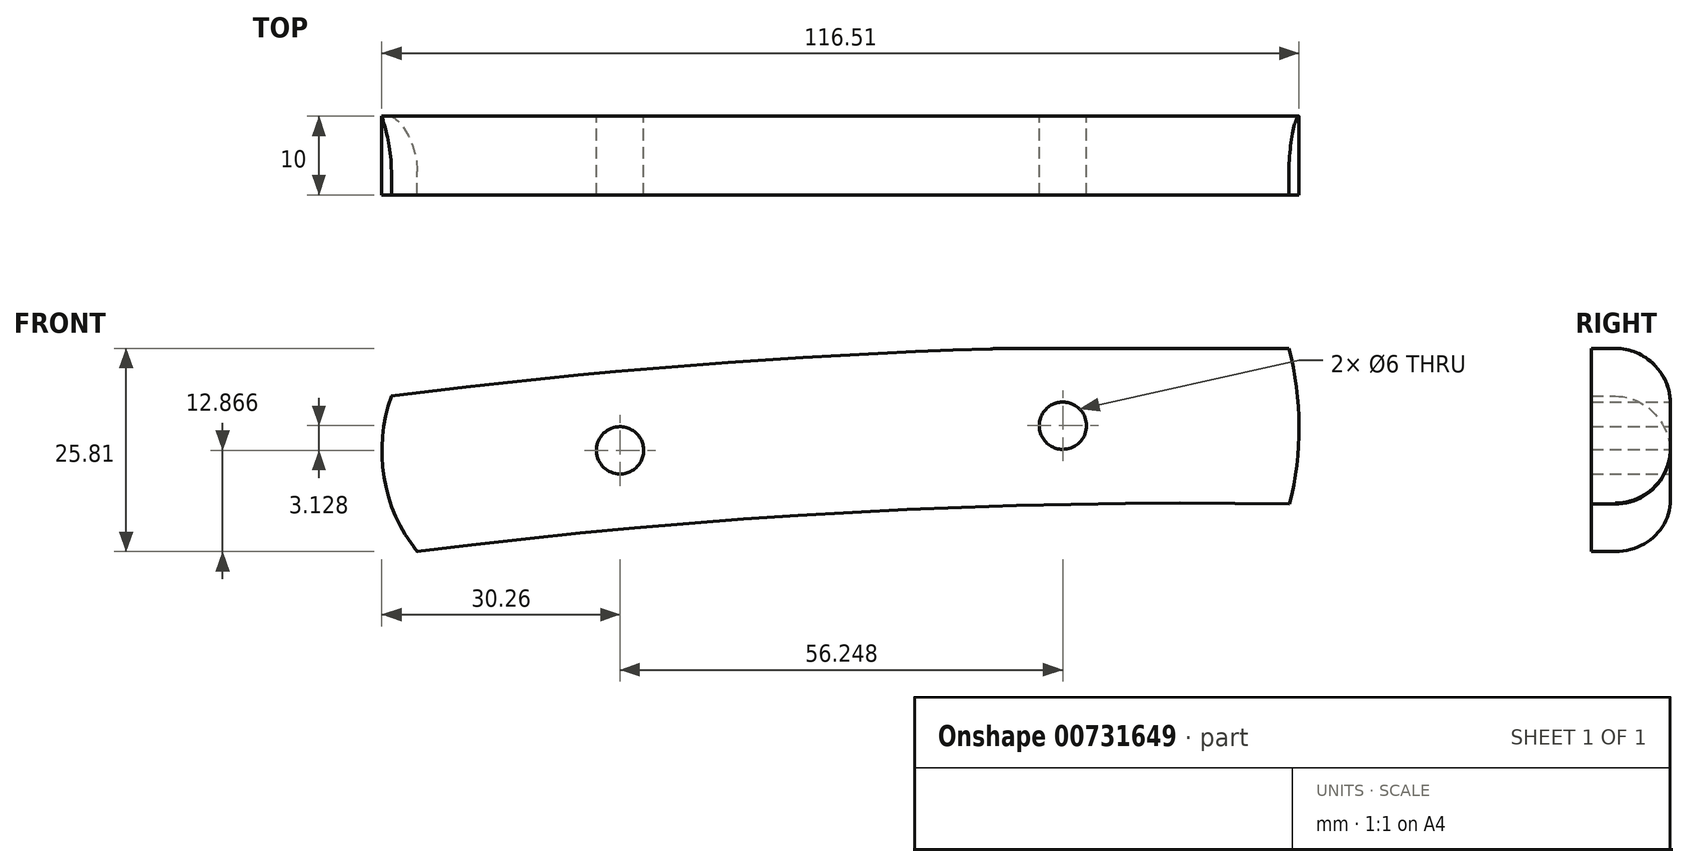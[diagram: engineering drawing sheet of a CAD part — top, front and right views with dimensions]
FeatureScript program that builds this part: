
annotation { "Feature Type Name" : "Feature", "Feature Type Description" : "" }
export const myFeature = defineFeature(function(context is Context, id is Id, definition is map)
    precondition{}
    {
        {
            var Q0;
            Q0=qCreatedBy(makeId("Front.planeOp"),FACE);
            var sketch = newSketch(context, id + "F0", { "sketchPlane" : qUnion([Q0])});
            skArc(sketch, "E0.0", {"start": v(13.6, 9.05) * mm, "mid": v(-24.53, 6.95) * mm, "end": v(-62.51, 3.04) * mm});
            skArc(sketch, "E1.0", {"start": v(16.72, 9.1) * mm, "mid": v(15.16, 9.09) * mm, "end": v(13.6, 9.05) * mm});
            skLineSegment(sketch, "E2.0", {"start": v(16.72, 9.1) * mm, "end": v(51.52, 9.1) * mm});
            skCircle(sketch, "E3.0", {"center": v(22.79, -0.72) * mm, "radius": 3 * mm});
            skCircle(sketch, "E4.0", {"center": v(-33.46, -3.84) * mm, "radius": 3 * mm});
            skArc(sketch, "E5.0", {"start": v(51.58, -10.67) * mm, "mid": v(-3.93, -11.72) * mm, "end": v(-59.23, -16.7) * mm});
            skArc(sketch, "E6.0", {"start": v(-62.51, 3.04) * mm, "mid": v(-63.44, -7.26) * mm, "end": v(-59.23, -16.7) * mm});
            skArc(sketch, "E7.0", {"start": v(51.58, -10.67) * mm, "mid": v(52.79, -0.78) * mm, "end": v(51.52, 9.1) * mm});
            skSolve(sketch);
        }
        {
            var Q0;
            Q0=makeQuery(id+"F0.imprint","IMPRINT",FACE,{"disambiguationData":[TD([[makeQuery(id+"F0.imprint","IMPRINT",EDGE,{"derivedFrom":sQuery(id+"F0.wireOp",EDGE,"E0.0")}),1.0]])]});
            extrude(context, id + "F1", {"entities" : qUnion([Q0]), "depth" : 10 * mm, "offsetDistance" : 25 * mm});
        }
        {
            var Q0;
            Q0=makeQuery(id+"F1.opExtrude","CAP_EDGE",EDGE,{"disambiguationData":[OSD([sQuery(id+"F0.wireOp",EDGE,"E0.0")])],"isStart":true});
            var Q1;
            Q1=makeQuery(id+"F1.opExtrude","CAP_EDGE",EDGE,{"disambiguationData":[OSD([sQuery(id+"F0.wireOp",EDGE,"E5.0")])],"isStart":true});
            fillet(context, id + "F2", {"entities" : qUnion([Q0, Q1]), "radius" : 7 * mm, "tangentPropagation" : true, "allowEdgeOverflow" : false});
        }
    });
